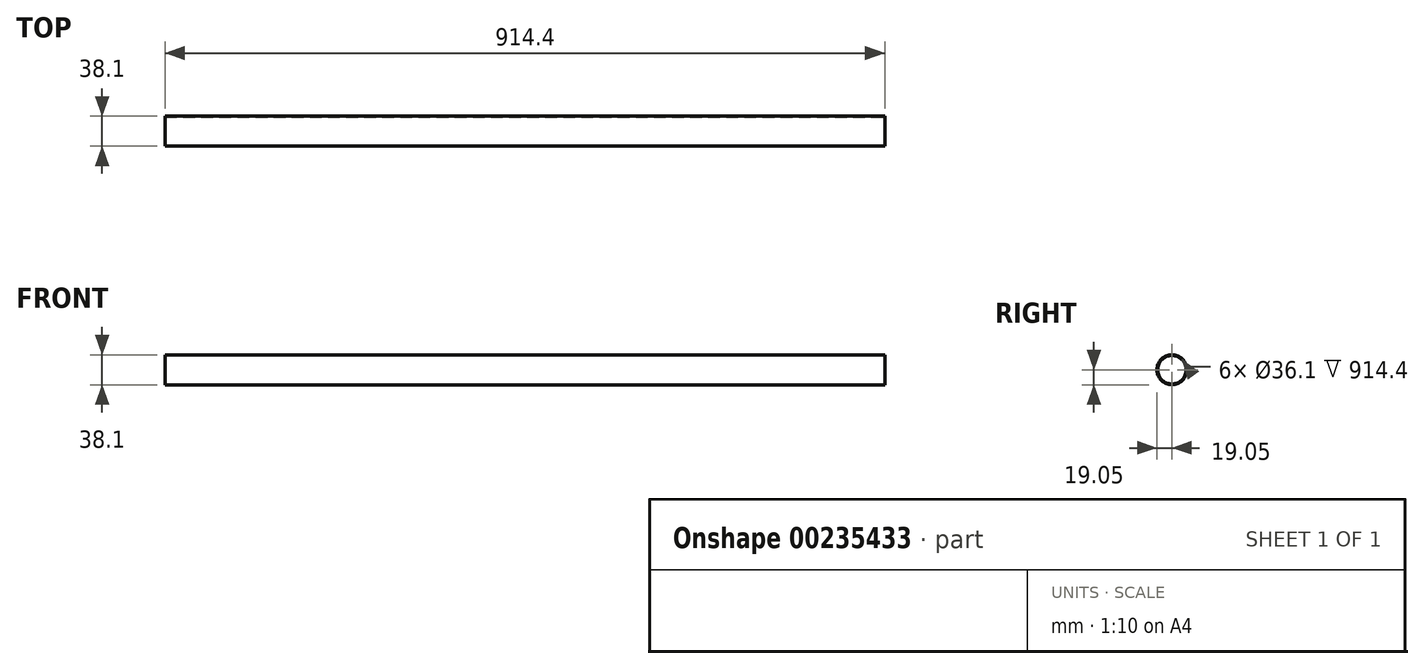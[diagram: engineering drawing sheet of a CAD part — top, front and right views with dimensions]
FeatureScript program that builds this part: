
annotation { "Feature Type Name" : "Feature", "Feature Type Description" : "" }
export const myFeature = defineFeature(function(context is Context, id is Id, definition is map)
    precondition{}
    {
        {
            var Q0;
            Q0=qCreatedBy(makeId("Top.planeOp"),FACE);
            var sketch = newSketch(context, id + "F0", { "sketchPlane" : qUnion([Q0])});
            skArc(sketch, "E0", {"start": v(457.2, 0) * mm, "mid": v(0, 29.97) * mm, "end": v(-457.2, 0) * mm, "construction": true});
            skLineSegment(sketch, "E1", {"start": v(-457.2, 0) * mm, "end": v(457.2, 0) * mm});
            skLineSegment(sketch, "E2", {"start": v(-457.2, 0) * mm, "end": v(0, -3472.78) * mm, "construction": true});
            skLineSegment(sketch, "E3", {"start": v(0, -3472.78) * mm, "end": v(457.2, 0) * mm, "construction": true});
            skSolve(sketch);
        }
        {
            var Q0;
            Q0=sQuery(id+"F0.wireOp",VERTEX,"E2.start");
            var Q1;
            Q1=sQuery(id+"F0.wireOp",EDGE,"E1");
            cPlane(context, id + "F1", {"entities" : qUnion([Q0, Q1]), "cplaneType" : CPlaneType.CURVE_POINT, "offset" : 25.4 * mm, "width" : 152.4 * mm, "height" : 152.4 * mm});
        }
        {
            var Q0;
            Q0=qCreatedBy(id+"F1.planeOp",FACE);
            var sketch = newSketch(context, id + "F2", { "sketchPlane" : qUnion([Q0])});
            skCircle(sketch, "E4", {"center": v(0, 0) * mm, "radius": 19.05 * mm});
            skCircle(sketch, "E5", {"center": v(0, 0) * mm, "radius": 18.05 * mm});
            skSolve(sketch);
        }
        {
            var Q0;
            Q0=makeQuery(id+"F2.imprint","IMPRINT",FACE,{"disambiguationData":[TD([[makeQuery(id+"F2.imprint","IMPRINT",EDGE,{"derivedFrom":sQuery(id+"F2.wireOp",EDGE,"E4")}),1.0]])]});
            var Q1;
            Q1=sQuery(id+"F0.wireOp",EDGE,"E1");
            sweep(context, id + "F3", {"profiles" : qUnion([Q0]), "path" : qUnion([Q1])});
        }
    });
